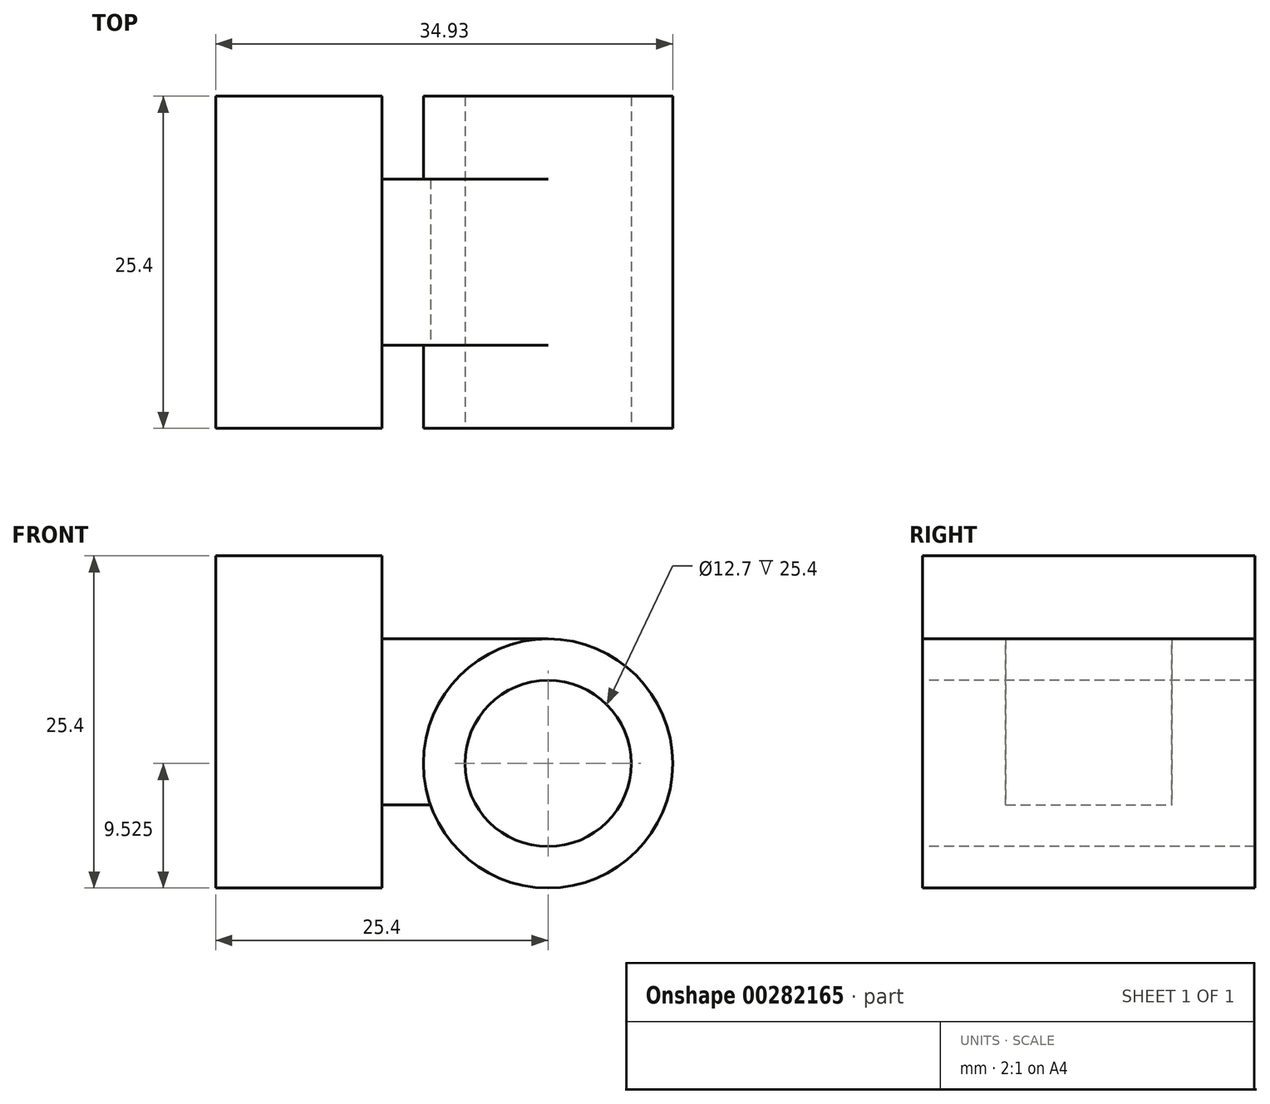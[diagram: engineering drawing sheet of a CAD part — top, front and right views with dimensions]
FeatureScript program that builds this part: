
annotation { "Feature Type Name" : "Feature", "Feature Type Description" : "" }
export const myFeature = defineFeature(function(context is Context, id is Id, definition is map)
    precondition{}
    {
        {
            var Q0;
            Q0=qCreatedBy(makeId("Right.planeOp"),FACE);
            var sketch = newSketch(context, id + "F0", { "sketchPlane" : qUnion([Q0])});
            skLineSegment(sketch, "E0.bottom", {"start": v(0, 0) * mm, "end": v(25.4, 0) * mm});
            skLineSegment(sketch, "E0.top", {"start": v(0, 25.4) * mm, "end": v(25.4, 25.4) * mm});
            skLineSegment(sketch, "E0.left", {"start": v(0, 0) * mm, "end": v(0, 25.4) * mm});
            skLineSegment(sketch, "E0.right", {"start": v(25.4, 0) * mm, "end": v(25.4, 25.4) * mm});
            skSolve(sketch);
        }
        {
            var Q0;
            Q0=makeQuery(id+"F0.imprint","IMPRINT",FACE,{"disambiguationData":[TD([[makeQuery(id+"F0.imprint","IMPRINT",EDGE,{"derivedFrom":sQuery(id+"F0.wireOp",EDGE,"E0.bottom")}),1.0]])]});
            extrude(context, id + "F1", {"entities" : qUnion([Q0]), "depth" : 12.7 * mm});
        }
        {
            var Q0;
            Q0=makeQuery(id+"F1.opExtrude","CAP_FACE",FACE,{"disambiguationData":[OSD([sQuery(id+"F0.wireOp",EDGE,"E0.bottom"),sQuery(id+"F0.wireOp",EDGE,"E0.top"),sQuery(id+"F0.wireOp",EDGE,"E0.left"),sQuery(id+"F0.wireOp",EDGE,"E0.right")])],"isStart":false});
            var sketch = newSketch(context, id + "F2", { "sketchPlane" : qUnion([Q0])});
            skLineSegment(sketch, "E1.bottom", {"start": v(6.35, 19.05) * mm, "end": v(19.05, 19.05) * mm});
            skLineSegment(sketch, "E1.top", {"start": v(6.35, 6.35) * mm, "end": v(19.05, 6.35) * mm});
            skLineSegment(sketch, "E1.left", {"start": v(6.35, 19.05) * mm, "end": v(6.35, 6.35) * mm});
            skLineSegment(sketch, "E1.right", {"start": v(19.05, 19.05) * mm, "end": v(19.05, 6.35) * mm});
            skSolve(sketch);
        }
        {
            var Q0;
            Q0=makeQuery(id+"F2.imprint","IMPRINT",FACE,{"disambiguationData":[TD([[makeQuery(id+"F2.imprint","IMPRINT",EDGE,{"derivedFrom":sQuery(id+"F2.wireOp",EDGE,"E1.bottom")}),-1.0]])]});
            extrude(context, id + "F3", {"entities" : qUnion([Q0]), "operationType" : NewBodyOperationType.ADD, "depth" : 12.7 * mm});
        }
        {
            var Q0;
            Q0=qCreatedBy(makeId("Front.planeOp"),FACE);
            var sketch = newSketch(context, id + "F4", { "sketchPlane" : qUnion([Q0])});
            skCircle(sketch, "E2", {"center": v(25.4, 9.53) * mm, "radius": 9.53 * mm});
            skSolve(sketch);
        }
        {
            var Q0;
            Q0=makeQuery(id+"F4.imprint","IMPRINT",FACE,{"disambiguationData":[TD([[makeQuery(id+"F4.imprint","IMPRINT",EDGE,{"derivedFrom":sQuery(id+"F4.wireOp",EDGE,"E2")}),1.0]])]});
            extrude(context, id + "F5", {"entities" : qUnion([Q0]), "operationType" : NewBodyOperationType.ADD, "oppositeDirection" : true, "depth" : 25.4 * mm});
        }
        {
            var Q0;
            Q0=makeQuery(id+"F5.opExtrude","CAP_FACE",FACE,{"disambiguationData":[OSD([sQuery(id+"F4.wireOp",EDGE,"E2")])],"isStart":true});
            var sketch = newSketch(context, id + "F6", { "sketchPlane" : qUnion([Q0])});
            skCircle(sketch, "E3", {"center": v(25.4, 9.53) * mm, "radius": 6.35 * mm});
            skSolve(sketch);
        }
        {
            var Q0;
            Q0=makeQuery(id+"F6.imprint","IMPRINT",FACE,{"disambiguationData":[TD([[makeQuery(id+"F6.imprint","IMPRINT",EDGE,{"derivedFrom":sQuery(id+"F6.wireOp",EDGE,"E3")}),1.0]])]});
            extrude(context, id + "F7", {"entities" : qUnion([Q0]), "operationType" : NewBodyOperationType.REMOVE, "oppositeDirection" : true, "depth" : 25.4 * mm});
        }
    });
